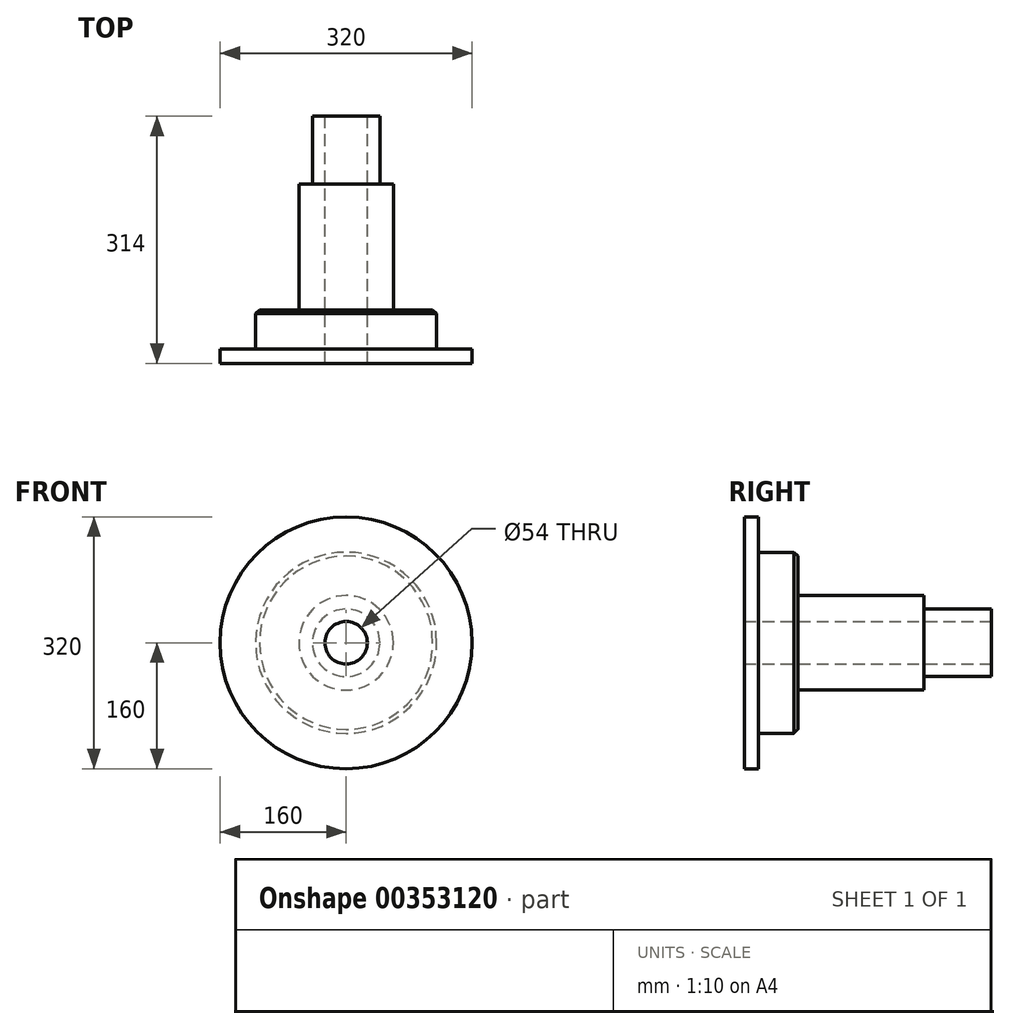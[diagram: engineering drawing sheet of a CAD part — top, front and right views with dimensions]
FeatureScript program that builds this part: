
annotation { "Feature Type Name" : "Feature", "Feature Type Description" : "" }
export const myFeature = defineFeature(function(context is Context, id is Id, definition is map)
    precondition{}
    {
        {
            var Q0;
            Q0=qCreatedBy(makeId("Front.planeOp"),FACE);
            var sketch = newSketch(context, id + "F0", { "sketchPlane" : qUnion([Q0])});
            skCircle(sketch, "E0", {"center": v(0, 0) * mm, "radius": 60 * mm});
            skSolve(sketch);
        }
        {
            var Q0;
            Q0 = qSketchRegion(id + "F0", true);
            extrude(context, id + "F1", {"entities" : qUnion([Q0]), "depth" : 160 * mm});
        }
        {
            var Q0;
            Q0=makeQuery(id+"F1.opExtrude","CAP_FACE",FACE,{"disambiguationData":[OSD([sQuery(id+"F0.wireOp",EDGE,"E0")])],"isStart":false});
            var sketch = newSketch(context, id + "F2", { "sketchPlane" : qUnion([Q0])});
            skCircle(sketch, "E1", {"center": v(0, 0) * mm, "radius": 115 * mm});
            skSolve(sketch);
        }
        {
            var Q0;
            Q0 = qSketchRegion(id + "F2", true);
            extrude(context, id + "F3", {"entities" : qUnion([Q0]), "operationType" : NewBodyOperationType.ADD, "depth" : 50 * mm});
        }
        {
            var Q0;
            Q0=makeQuery(id+"F3.opExtrude","CAP_FACE",FACE,{"disambiguationData":[OSD([sQuery(id+"F2.wireOp",EDGE,"E1")])],"isStart":false});
            var sketch = newSketch(context, id + "F4", { "sketchPlane" : qUnion([Q0])});
            skCircle(sketch, "E2", {"center": v(0, 0) * mm, "radius": 160 * mm});
            skSolve(sketch);
        }
        {
            var Q0;
            Q0 = qSketchRegion(id + "F4", true);
            extrude(context, id + "F5", {"entities" : qUnion([Q0]), "operationType" : NewBodyOperationType.ADD, "depth" : 18 * mm});
        }
        {
            var Q0;
            Q0=makeQuery(id+"F3.opExtrude","CAP_EDGE",EDGE,{"disambiguationData":[OSD([sQuery(id+"F2.wireOp",EDGE,"E1")])],"isStart":true});
            chamfer(context, id + "F6", {"entities" : qUnion([Q0]), "width" : 5 * mm, "tangentPropagation" : true});
        }
        {
            var Q0;
            Q0=makeQuery(id+"F1.opExtrude","CAP_FACE",FACE,{"disambiguationData":[OSD([sQuery(id+"F0.wireOp",EDGE,"E0")])],"isStart":true});
            var sketch = newSketch(context, id + "F7", { "sketchPlane" : qUnion([Q0])});
            skCircle(sketch, "E3", {"center": v(0, 0) * mm, "radius": 42.88 * mm});
            skSolve(sketch);
        }
        {
            var Q0;
            Q0 = qSketchRegion(id + "F7", true);
            extrude(context, id + "F8", {"entities" : qUnion([Q0]), "operationType" : NewBodyOperationType.ADD, "depth" : 86 * mm});
        }
        {
            var Q0;
            Q0=makeQuery(id+"F8.opExtrude","CAP_FACE",FACE,{"disambiguationData":[OSD([sQuery(id+"F7.wireOp",EDGE,"E3")])],"isStart":false});
            var sketch = newSketch(context, id + "F9", { "sketchPlane" : qUnion([Q0])});
            skCircle(sketch, "E4", {"center": v(0, 0) * mm, "radius": 27 * mm});
            skSolve(sketch);
        }
        {
            var Q0;
            Q0 = qSketchRegion(id + "F9", true);
            extrude(context, id + "F10", {"entities" : qUnion([Q0]), "operationType" : NewBodyOperationType.REMOVE, "oppositeDirection" : true, "depth" : 430 * mm});
        }
    });
